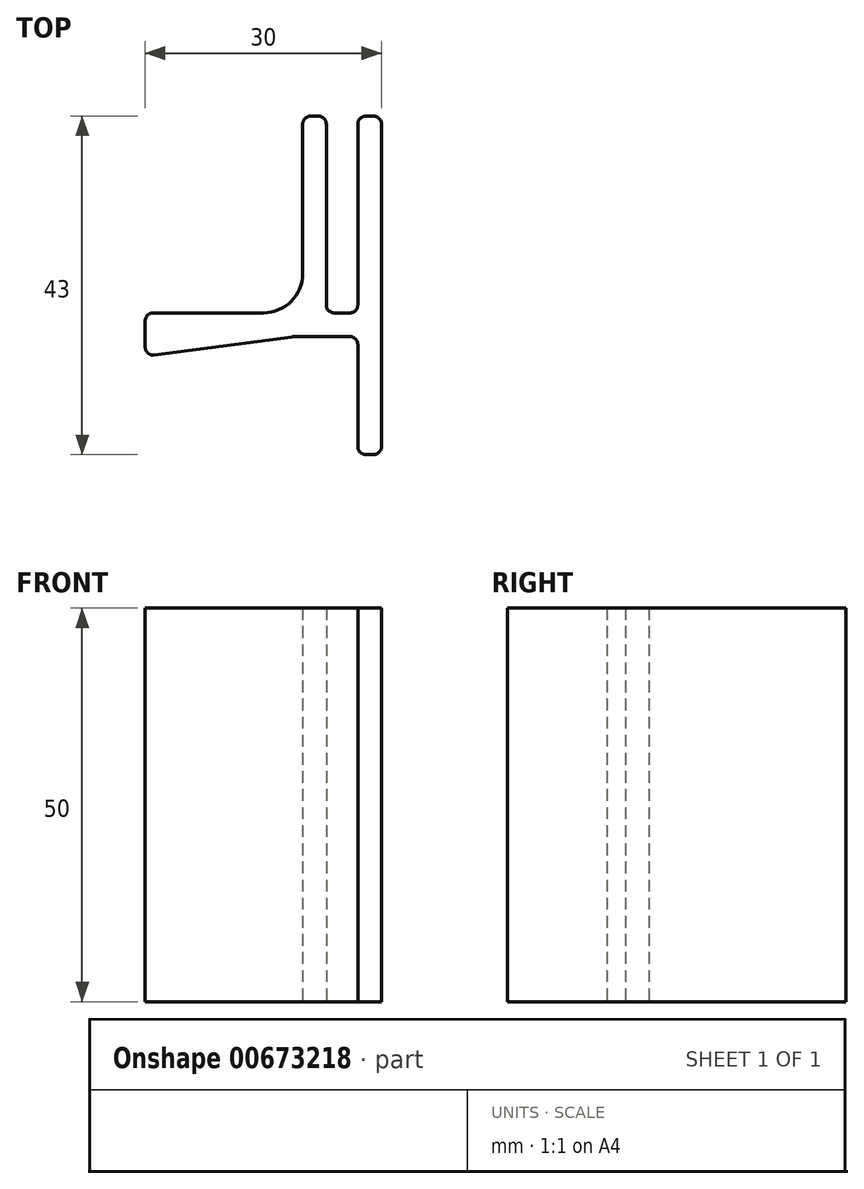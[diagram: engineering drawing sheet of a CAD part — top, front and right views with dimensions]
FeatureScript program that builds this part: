
annotation { "Feature Type Name" : "Feature", "Feature Type Description" : "" }
export const myFeature = defineFeature(function(context is Context, id is Id, definition is map)
    precondition{}
    {
        {
            var Q0;
            Q0=qCreatedBy(makeId("Top.planeOp"),FACE);
            var sketch = newSketch(context, id + "F0", { "sketchPlane" : qUnion([Q0])});
            skLineSegment(sketch, "E0", {"start": v(0, 0) * mm, "end": v(0, 15) * mm});
            skLineSegment(sketch, "E1", {"start": v(0, 15) * mm, "end": v(-27, 15) * mm});
            skLineSegment(sketch, "E2", {"start": v(-27, 15) * mm, "end": v(-27, 18) * mm});
            skLineSegment(sketch, "E3", {"start": v(-27, 18) * mm, "end": v(-7, 18) * mm});
            skLineSegment(sketch, "E4", {"start": v(-7, 18) * mm, "end": v(-7, 43) * mm});
            skLineSegment(sketch, "E5", {"start": v(-7, 43) * mm, "end": v(-4, 43) * mm});
            skLineSegment(sketch, "E6", {"start": v(-4, 43) * mm, "end": v(-4, 18) * mm});
            skLineSegment(sketch, "E7", {"start": v(-4, 18) * mm, "end": v(0, 18) * mm});
            skLineSegment(sketch, "E8", {"start": v(0, 18) * mm, "end": v(0, 43) * mm});
            skLineSegment(sketch, "E9", {"start": v(0, 43) * mm, "end": v(0, 43) * mm});
            skLineSegment(sketch, "E10", {"start": v(0, 43) * mm, "end": v(3, 43) * mm});
            skLineSegment(sketch, "E11", {"start": v(3, 43) * mm, "end": v(3, 0) * mm});
            skLineSegment(sketch, "E12", {"start": v(3, 0) * mm, "end": v(0, 0) * mm});
            skLineSegment(sketch, "E13", {"start": v(-8, 15) * mm, "end": v(-27, 12.5) * mm});
            skLineSegment(sketch, "E14", {"start": v(-27, 12.5) * mm, "end": v(-27, 15) * mm});
            skSolve(sketch);
        }
        {
            var Q0;
            Q0 = qSketchRegion(id + "F0", true);
            extrude(context, id + "F1", {"entities" : qUnion([Q0]), "depth" : 50 * mm, "offsetDistance" : 25 * mm});
        }
        {
            var Q0;
            Q0=makeQuery(id+"F1.opExtrude","SWEPT_EDGE",EDGE,{"disambiguationData":[OSD([sQuery(id+"F0.wireOp",EDGE,"E1"),sQuery(id+"F0.wireOp",EDGE,"E13")])]});
            var Q1;
            Q1=makeQuery(id+"F1.opExtrude","SWEPT_EDGE",EDGE,{"disambiguationData":[OSD([sQuery(id+"F0.wireOp",EDGE,"E3"),sQuery(id+"F0.wireOp",EDGE,"E4")])]});
            fillet(context, id + "F2", {"entities" : qUnion([Q0, Q1]), "radius" : 5 * mm, "tangentPropagation" : true, "allowEdgeOverflow" : false});
        }
        {
            var Q0;
            Q0=makeQuery(id+"F1.opExtrude","SWEPT_EDGE",EDGE,{"disambiguationData":[OSD([sQuery(id+"F0.wireOp",EDGE,"E4"),sQuery(id+"F0.wireOp",EDGE,"E5")])]});
            var Q1;
            Q1=makeQuery(id+"F1.opExtrude","SWEPT_EDGE",EDGE,{"disambiguationData":[OSD([sQuery(id+"F0.wireOp",EDGE,"E5"),sQuery(id+"F0.wireOp",EDGE,"E6")])]});
            var Q2;
            Q2=makeQuery(id+"F1.opExtrude","SWEPT_EDGE",EDGE,{"disambiguationData":[OSD([sQuery(id+"F0.wireOp",EDGE,"E8"),sQuery(id+"F0.wireOp",EDGE,"E10")])]});
            var Q3;
            Q3=makeQuery(id+"F1.opExtrude","SWEPT_EDGE",EDGE,{"disambiguationData":[OSD([sQuery(id+"F0.wireOp",EDGE,"E10"),sQuery(id+"F0.wireOp",EDGE,"E11")])]});
            var Q4;
            Q4=makeQuery(id+"F1.opExtrude","SWEPT_EDGE",EDGE,{"disambiguationData":[OSD([sQuery(id+"F0.wireOp",EDGE,"E0"),sQuery(id+"F0.wireOp",EDGE,"E12")])]});
            var Q5;
            Q5=makeQuery(id+"F1.opExtrude","SWEPT_EDGE",EDGE,{"disambiguationData":[OSD([sQuery(id+"F0.wireOp",EDGE,"E11"),sQuery(id+"F0.wireOp",EDGE,"E12")])]});
            var Q6;
            Q6=makeQuery(id+"F1.opExtrude","SWEPT_EDGE",EDGE,{"disambiguationData":[OSD([sQuery(id+"F0.wireOp",EDGE,"E0"),sQuery(id+"F0.wireOp",EDGE,"E1")])]});
            var Q7;
            Q7=makeQuery(id+"F1.opExtrude","SWEPT_EDGE",EDGE,{"disambiguationData":[OSD([sQuery(id+"F0.wireOp",EDGE,"E6"),sQuery(id+"F0.wireOp",EDGE,"E7")])]});
            var Q8;
            Q8=makeQuery(id+"F1.opExtrude","SWEPT_EDGE",EDGE,{"disambiguationData":[OSD([sQuery(id+"F0.wireOp",EDGE,"E7"),sQuery(id+"F0.wireOp",EDGE,"E8")])]});
            var Q9;
            Q9=makeQuery(id+"F1.opExtrude","SWEPT_EDGE",EDGE,{"disambiguationData":[OSD([sQuery(id+"F0.wireOp",EDGE,"E13"),sQuery(id+"F0.wireOp",EDGE,"E14")])]});
            var Q10;
            Q10=makeQuery(id+"F1.opExtrude","SWEPT_EDGE",EDGE,{"disambiguationData":[OSD([sQuery(id+"F0.wireOp",EDGE,"E2"),sQuery(id+"F0.wireOp",EDGE,"E3")])]});
            fillet(context, id + "F3", {"entities" : qUnion([Q0, Q1, Q2, Q3, Q4, Q5, Q6, Q7, Q8, Q9, Q10]), "radius" : 1 * mm, "tangentPropagation" : true, "allowEdgeOverflow" : false});
        }
    });
